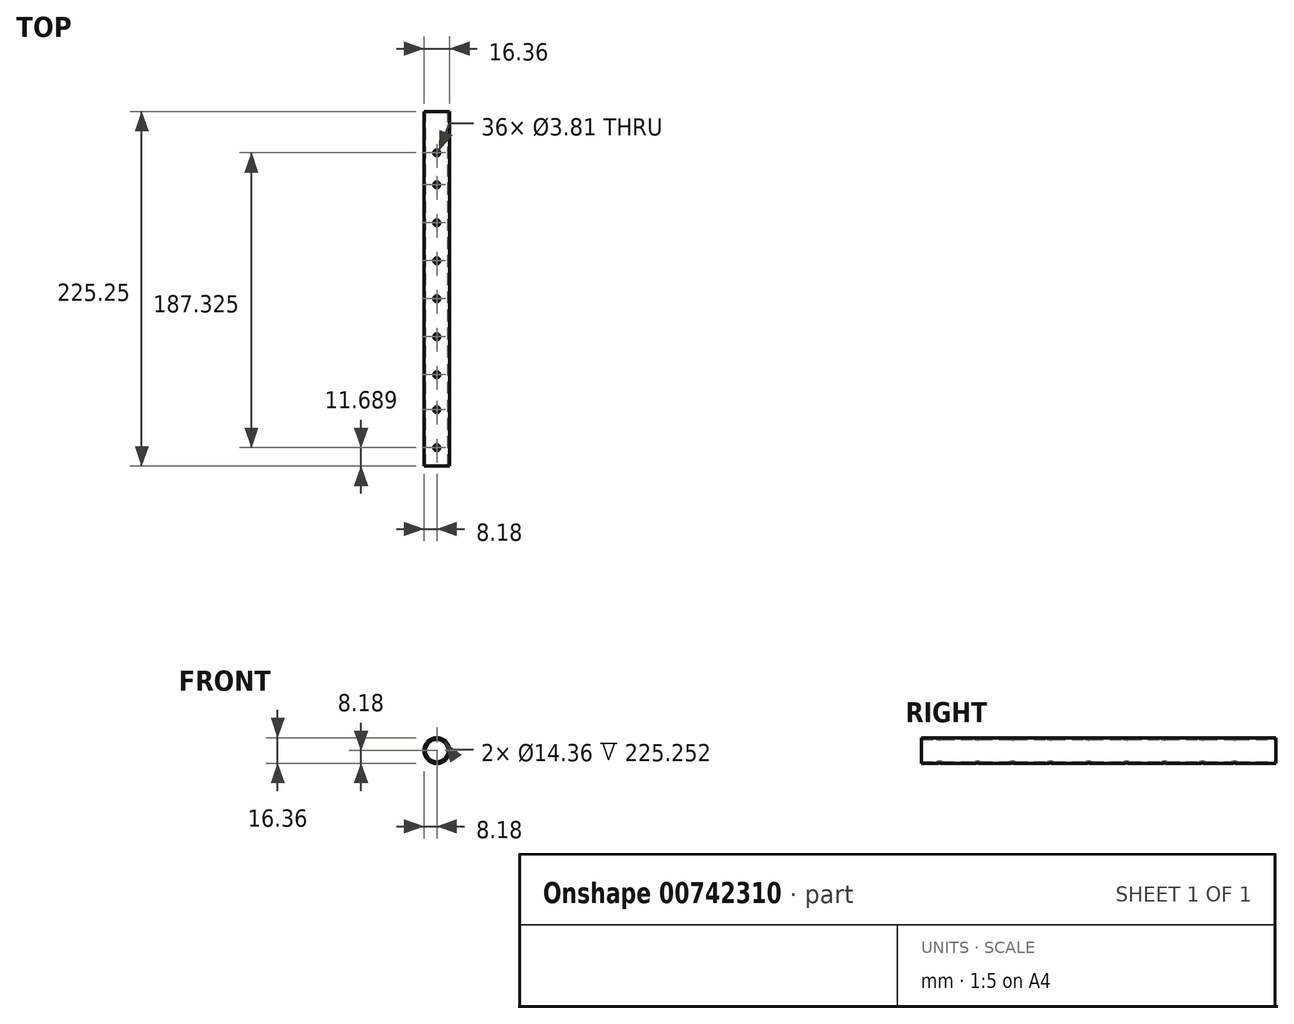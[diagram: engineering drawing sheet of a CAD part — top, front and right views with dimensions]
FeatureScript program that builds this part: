
annotation { "Feature Type Name" : "Feature", "Feature Type Description" : "" }
export const myFeature = defineFeature(function(context is Context, id is Id, definition is map)
    precondition{}
    {
        {
            var Q0;
            Q0=qCreatedBy(makeId("Top.planeOp"),FACE);
            var sketch = newSketch(context, id + "F0", { "sketchPlane" : qUnion([Q0])});
            skCircle(sketch, "E0", {"center": v(0, -46.56) * mm, "radius": 1.9 * mm});
            skCircle(sketch, "E1", {"center": v(0, -94.82) * mm, "radius": 1.9 * mm});
            skCircle(sketch, "E2", {"center": v(0, -143.08) * mm, "radius": 1.9 * mm});
            skCircle(sketch, "E3", {"center": v(0, -189.43) * mm, "radius": 1.9 * mm});
            skLineSegment(sketch, "E4.bottom", {"start": v(-10.08, 0) * mm, "end": v(9.43, 0) * mm});
            skLineSegment(sketch, "E4.top", {"start": v(-10.08, -225.25) * mm, "end": v(9.43, -225.25) * mm});
            skLineSegment(sketch, "E4.left", {"start": v(-10.08, 0) * mm, "end": v(-10.08, -225.25) * mm});
            skLineSegment(sketch, "E4.right", {"start": v(9.43, 0) * mm, "end": v(9.43, -225.25) * mm});
            skCircle(sketch, "E5", {"center": v(0, -167.2) * mm, "radius": 1.9 * mm});
            skCircle(sketch, "E6", {"center": v(0, -118.95) * mm, "radius": 1.9 * mm});
            skCircle(sketch, "E7", {"center": v(0, -70.69) * mm, "radius": 1.9 * mm});
            skCircle(sketch, "E8", {"center": v(0, -26.24) * mm, "radius": 1.9 * mm});
            skCircle(sketch, "E9", {"center": v(0, -213.56) * mm, "radius": 1.9 * mm});
            skSolve(sketch);
        }
        {
            var Q0;
            Q0=qCreatedBy(makeId("Front.planeOp"),FACE);
            var sketch = newSketch(context, id + "F1", { "sketchPlane" : qUnion([Q0])});
            skCircle(sketch, "E10", {"center": v(0, 0) * mm, "radius": 8.18 * mm});
            skCircle(sketch, "E11", {"center": v(0, 0) * mm, "radius": 7.18 * mm});
            skSolve(sketch);
        }
        {
            var Q0;
            Q0=makeQuery(id+"F0.imprint","IMPRINT",FACE,{"disambiguationData":[TD([[makeQuery(id+"F0.imprint","IMPRINT",EDGE,{"derivedFrom":sQuery(id+"F0.wireOp",EDGE,"E0")}),-1.0]])]});
            extrude(context, id + "F2", {"entities" : qUnion([Q0]), "endBound" : BoundingType.SYMMETRIC, "depth" : 25.4 * mm, "offsetDistance" : 25.4 * mm});
        }
        {
            var Q0;
            Q0=makeQuery(id+"F1.imprint","IMPRINT",FACE,{"disambiguationData":[TD([[makeQuery(id+"F1.imprint","IMPRINT",EDGE,{"derivedFrom":sQuery(id+"F1.wireOp",EDGE,"E10")}),1.0]])]});
            extrude(context, id + "F3", {"entities" : qUnion([Q0]), "operationType" : NewBodyOperationType.INTERSECT, "endBound" : BoundingType.SYMMETRIC, "depth" : 497.33 * mm, "offsetDistance" : 25.4 * mm});
        }
    });
